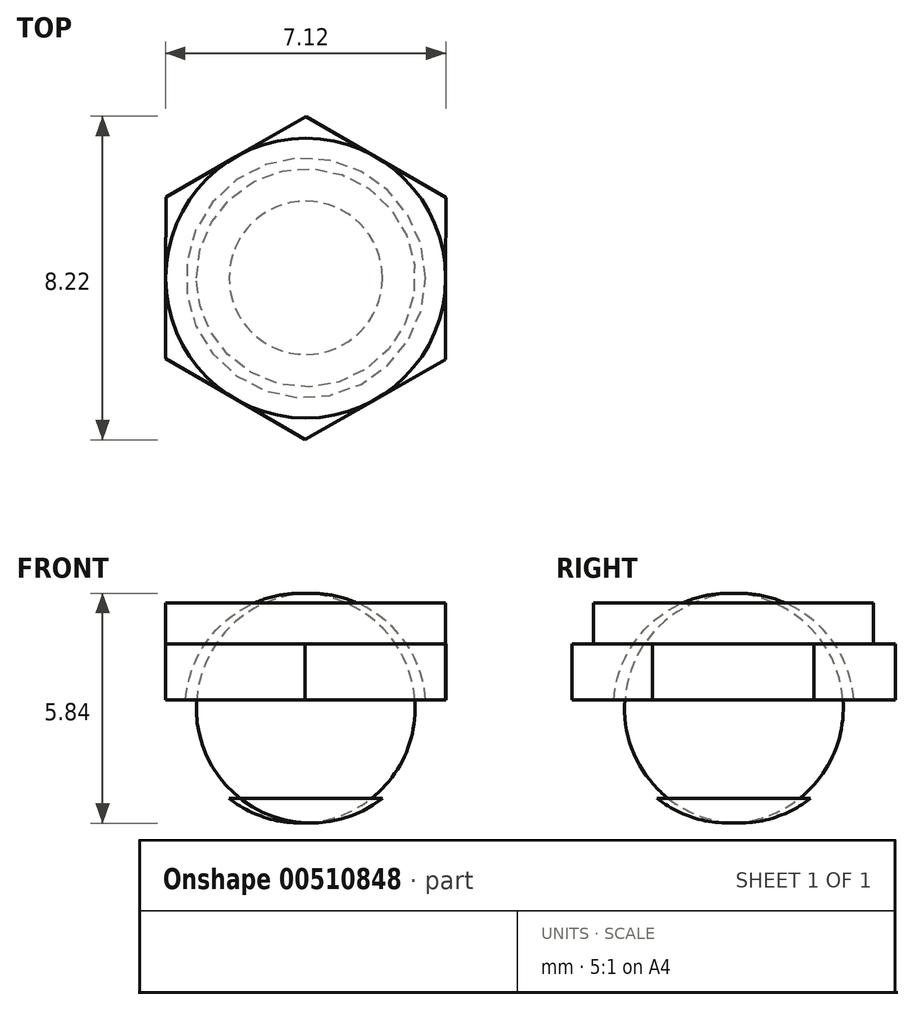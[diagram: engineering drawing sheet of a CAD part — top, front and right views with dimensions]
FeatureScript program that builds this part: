
annotation { "Feature Type Name" : "Feature", "Feature Type Description" : "" }
export const myFeature = defineFeature(function(context is Context, id is Id, definition is map)
    precondition{}
    {
        {
            var Q0;
            Q0=qCreatedBy(makeId("Top.planeOp"),FACE);
            var sketch = newSketch(context, id + "F0", { "sketchPlane" : qUnion([Q0])});
            skCircle(sketch, "E0", {"center": v(0, 0) * mm, "radius": 3.56 * mm});
            skSolve(sketch);
        }
        {
            var Q0;
            Q0=makeQuery(id+"F0.imprint","IMPRINT",FACE,{"disambiguationData":[TD([[makeQuery(id+"F0.imprint","IMPRINT",EDGE,{"derivedFrom":sQuery(id+"F0.wireOp",EDGE,"E0")}),1.0]])]});
            extrude(context, id + "F1", {"entities" : qUnion([Q0]), "oppositeDirection" : true, "depth" : 1.04 * mm});
        }
        {
            var Q0;
            Q0=makeQuery(id+"F1.opExtrude","CAP_FACE",FACE,{"disambiguationData":[OSD([sQuery(id+"F0.wireOp",EDGE,"E0")])],"isStart":false});
            var sketch = newSketch(context, id + "F2", { "sketchPlane" : qUnion([Q0])});
            skCircle(sketch, "E1.cCircle", {"center": v(0, 0) * mm, "radius": 3.56 * mm, "construction": true});
            skLineSegment(sketch, "E1.0", {"start": v(3.56, -2.04) * mm, "end": v(0.01, -4.1) * mm});
            skLineSegment(sketch, "E1.1", {"start": v(0.01, -4.1) * mm, "end": v(-3.55, -2.06) * mm});
            skLineSegment(sketch, "E1.2", {"start": v(-3.55, -2.06) * mm, "end": v(-3.56, 2.04) * mm});
            skLineSegment(sketch, "E1.3", {"start": v(-3.56, 2.04) * mm, "end": v(-0.01, 4.1) * mm});
            skLineSegment(sketch, "E1.4", {"start": v(-0.01, 4.1) * mm, "end": v(3.55, 2.06) * mm});
            skLineSegment(sketch, "E1.5", {"start": v(3.55, 2.06) * mm, "end": v(3.56, -2.04) * mm});
            skPoint(sketch, "E1.0.midPoint", {"position": v(1.79, -3.07) * mm});
            skSolve(sketch);
        }
        {
            var Q0;
            Q0=qSketchRegion(id+"F2",true);
            extrude(context, id + "F3", {"entities" : qUnion([Q0]), "operationType" : NewBodyOperationType.ADD, "depth" : 1.42 * mm});
        }
        {
            var Q0;
            Q0=qCreatedBy(makeId("Right.planeOp"),FACE);
            var sketch = newSketch(context, id + "F4", { "sketchPlane" : qUnion([Q0])});
            skLineSegment(sketch, "E2", {"start": v(0, -4.97) * mm, "end": v(1.95, -4.97) * mm});
            skArc(sketch, "E3", {"start": v(1.95, -4.97) * mm, "mid": v(2.82, -3.85) * mm, "end": v(3.05, -2.46) * mm});
            skLineSegment(sketch, "E4", {"start": v(3.05, -2.46) * mm, "end": v(0, -2.46) * mm});
            skLineSegment(sketch, "E5", {"start": v(0, -2.46) * mm, "end": v(0, -4.97) * mm});
            skSolve(sketch);
        }
        {
            var Q0;
            Q0=makeQuery(id+"F4.imprint","IMPRINT",FACE,{"disambiguationData":[TD([[makeQuery(id+"F4.imprint","IMPRINT",EDGE,{"derivedFrom":sQuery(id+"F4.wireOp",EDGE,"E2")}),1.0]])]});
            var Q1;
            Q1=sQuery(id+"F4.wireOp",EDGE,"E5");
            revolve(context, id + "F5", {"operationType" : NewBodyOperationType.ADD, "entities" : qUnion([Q0]), "axis" : qUnion([Q1]), "revolveType" : RevolveType.FULL});
        }
    });
